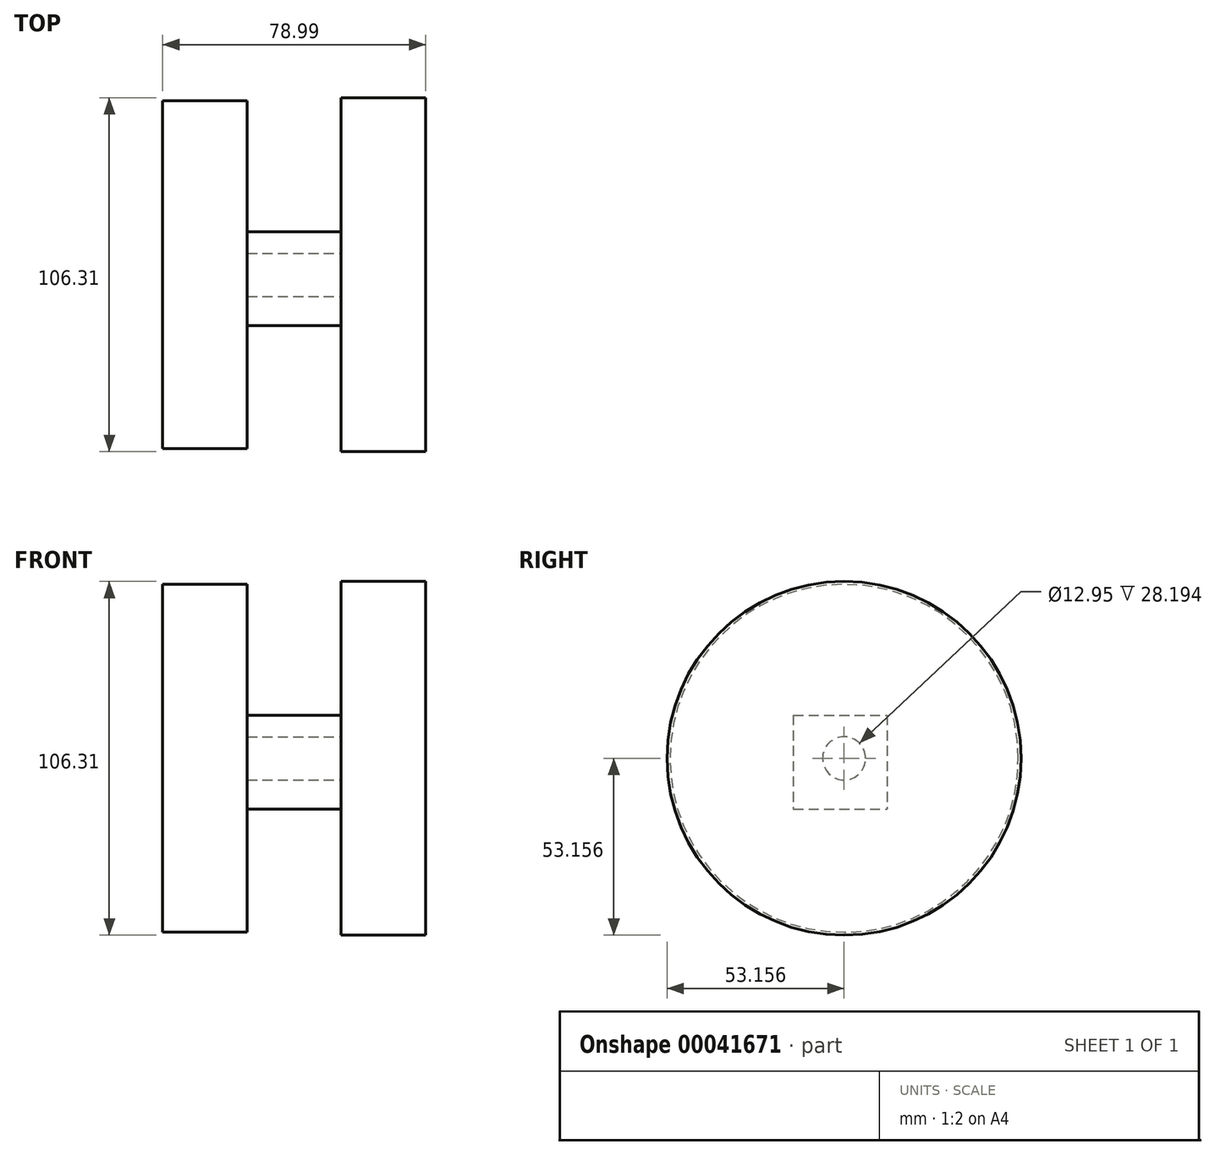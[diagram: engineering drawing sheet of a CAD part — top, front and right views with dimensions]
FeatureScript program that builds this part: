
annotation { "Feature Type Name" : "Feature", "Feature Type Description" : "" }
export const myFeature = defineFeature(function(context is Context, id is Id, definition is map)
    precondition{}
    {
        {
            var Q0;
            Q0=qCreatedBy(makeId("Front.planeOp"),FACE);
            var sketch = newSketch(context, id + "F0", { "sketchPlane" : qUnion([Q0])});
            skLineSegment(sketch, "E0.bottom", {"start": v(0, 0) * mm, "end": v(-28.2, 0) * mm});
            skLineSegment(sketch, "E0.top", {"start": v(0, -28.2) * mm, "end": v(-28.2, -28.2) * mm});
            skLineSegment(sketch, "E0.left", {"start": v(0, 0) * mm, "end": v(0, -28.2) * mm});
            skLineSegment(sketch, "E0.right", {"start": v(-28.2, 0) * mm, "end": v(-28.2, -28.2) * mm});
            skSolve(sketch);
        }
        {
            var Q0;
            Q0 = qSketchRegion(id + "F0", true);
            extrude(context, id + "F1", {"entities" : qUnion([Q0]), "depth" : 28.2 * mm});
        }
        {
            var Q0;
            Q0=makeQuery(id+"F1.opExtrude","SWEPT_FACE",FACE,{"disambiguationData":[OSD([sQuery(id+"F0.wireOp",EDGE,"E0.left")])]});
            var sketch = newSketch(context, id + "F2", { "sketchPlane" : qUnion([Q0])});
            skCircle(sketch, "E1", {"center": v(-12.95, -12.95) * mm, "radius": 6.48 * mm});
            skSolve(sketch);
        }
        {
            var Q0;
            Q0 = qSketchRegion(id + "F2", true);
            extrude(context, id + "F3", {"entities" : qUnion([Q0]), "operationType" : NewBodyOperationType.REMOVE, "endBound" : BoundingType.THROUGH_ALL, "oppositeDirection" : true, "depth" : 25.4 * mm});
        }
        {
            var Q0;
            Q0=makeQuery(id+"F1.opExtrude","SWEPT_FACE",FACE,{"disambiguationData":[OSD([sQuery(id+"F0.wireOp",EDGE,"E0.left")])]});
            var sketch = newSketch(context, id + "F4", { "sketchPlane" : qUnion([Q0])});
            skCircle(sketch, "E2", {"center": v(-12.95, -12.95) * mm, "radius": 53.16 * mm});
            skSolve(sketch);
        }
        {
            var Q0;
            Q0 = qSketchRegion(id + "F4", true);
            extrude(context, id + "F5", {"entities" : qUnion([Q0]), "operationType" : NewBodyOperationType.ADD, "depth" : 25.4 * mm});
        }
        {
            var Q0;
            Q0=makeQuery(id+"F1.opExtrude","SWEPT_FACE",FACE,{"disambiguationData":[OSD([sQuery(id+"F0.wireOp",EDGE,"E0.right")])]});
            var sketch = newSketch(context, id + "F6", { "sketchPlane" : qUnion([Q0])});
            skCircle(sketch, "E3", {"center": v(12.95, -12.95) * mm, "radius": 52.28 * mm});
            skSolve(sketch);
        }
        {
            var Q0;
            Q0 = qSketchRegion(id + "F6", true);
            extrude(context, id + "F7", {"entities" : qUnion([Q0]), "operationType" : NewBodyOperationType.ADD, "depth" : 25.4 * mm});
        }
    });
